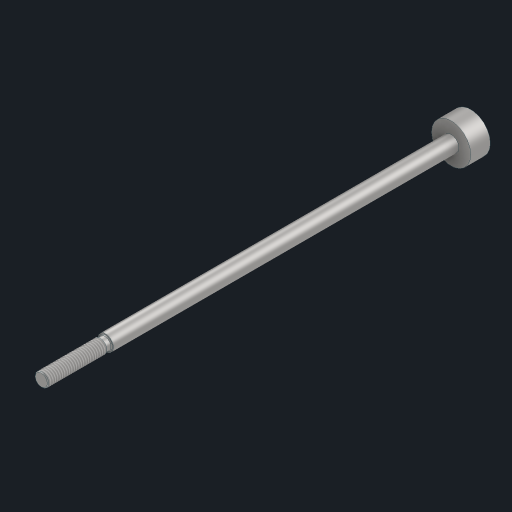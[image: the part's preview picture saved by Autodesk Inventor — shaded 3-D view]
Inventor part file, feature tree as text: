
AUTODESK INVENTOR PART (.ipt)
format: ipt  version: 2023 (Build 270158030, 158C)  size: 125,952 bytes
history: mixed  units: in
note: dims shown in document units (in); Inventor stores cm internally (conversion verified against a paired STEP export)
features: thread x2, imported_body x1
ambient origin geometry x8: Origin, YZ Plane, XZ Plane, XY Plane, X Axis, Y Axis, Z Axis, Center Point
bodies: Solid1 (imported_parasolid)
feature tree (3):
  thread  "Thread1"  [1 undecoded]
  thread  "Threads"  [1 undecoded]
  imported_body  NMx_Import_Brep_tag  [imported B-rep: ~11 faces, bbox_mm=[7.0, 0.0, 109.434]]
note: 2 required parameter values undecoded (feature->parameter linkage not recoverable at this tier; creation-order binding heuristic only, values carry confidence <= 0.55)
